# Revit family: KAPI
name_source: partatom
category: Doors
revit_build: Autodesk Revit 2015 (Build: 20140322_1515(x64)
units: mm (PartAtom-declared; Revit-internal decimal feet)

## types (4) — shared parameters
Analytic Construction = Metal
Construction Type Id = MDOOR
Door Material = Door - Panel
Frame Material = Door - Frame
Function = Interior
Heat Transfer Coefficient (U) = 3.7021 W/(m²·K)
Height = 2200 mm
Rough Height = 2200 mm
Thermal Resistance (R) = 0.2701 (m²·K)/W
Thickness = 51 mm
Trim Projection Ext = 25 mm  [stored 0.082021 ft]
Trim Projection Int = 25 mm  [stored 0.082021 ft]
Trim Width = 76 mm
Wall Closure = By host
aci = 45.00°
zero-valued in all types: Solar Heat Gain Coefficient, Visual Light Transmittance

## per-type parameters (varying)
| type | Width | Yay |
| 0800 x 2200mm | 800 mm  [stored 2.62467 ft] | 750 mm  [stored 2.46063 ft] |
| 0900 x 2200mm | 900 mm  [stored 2.95276 ft] | 850 mm |
| 1000 x 2200mm | 1000 mm | 950 mm |
| 1000 x 2200mm 2 | 1200 mm | 1150 mm |

note: [stored X ft] marks values corroborated as IEEE doubles in the binary element streams (Revit-internal decimal feet)

## geometry (parser evidence)
native form markers: Sweep x1
no freeform markers — native parametric forms only
